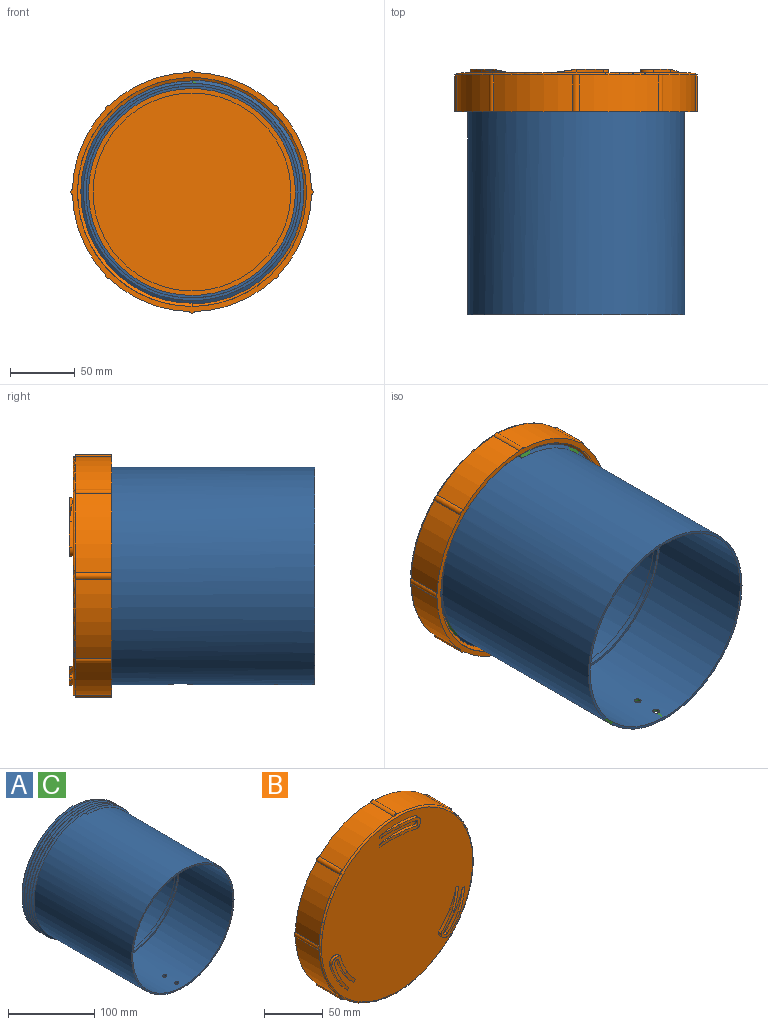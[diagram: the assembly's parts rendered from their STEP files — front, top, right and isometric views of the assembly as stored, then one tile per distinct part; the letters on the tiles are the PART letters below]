
ASSEMBLY  parts=3 mates=1
PART A: 20 faces, bbox 199.8x180x173 mm
  f0: cylinder r=84mm len=168mm, axis (0,1,0), area 83625.4mm2, adj f5,f8,f14,f15,f17,f18,f19
  f1: cylinder r=84mm len=168mm, axis (0,1,0), area 1055.6mm2, adj f2,f9,f13,f16
  f2: cylinder r=84mm len=168mm, axis (0,1,0), area 587.6mm2, adj f1,f3,f15,f16
  f3: cylinder r=84mm len=168mm, axis (0,1,0), area 587.6mm2, adj f2,f4,f15,f16
  f4: cylinder r=84mm len=168mm, axis (0,1,0), area 587.6mm2, adj f3,f5,f15,f16
  f5: cylinder r=84mm len=168mm, axis (0,1,0), area 587.6mm2, adj f0,f4,f15,f16
  f6: cylinder r=82mm len=164mm, axis (0,1,0), area 45300.5mm2, adj f8,f10,f18,f19
  f7: cylinder r=82mm len=164mm, axis (0,1,0), area 45025.2mm2, adj f9,f11,f17
  f8: plane 168x168mm, normal (0,-1,0), area 1043mm2, adj f0,f6
  f9: plane 168x168mm, normal (0,1,0), area 1043mm2, adj f1,f7
  f10: plane 164x164mm, normal (0,-1,0), area 1017.9mm2, adj f6,f12
  f11: plane 164x164mm, normal (0,1,0), area 1017.9mm2, adj f7,f12
  f12: cylinder r=80mm len=160mm, axis (0,1,0), area 2010.6mm2, adj f10,f11
  f13: plane 2.89x2.5mm, normal (1,0,0), area 3.6mm2, adj f1,f15,f16
  f14: plane 2.89x2.5mm, normal (-1,0,0), area 3.6mm2, adj f0,f15,f16
  f15: bspline ~199.76x173mm, area 7725.5mm2, adj f0,f2,f3,f4,f5,f13,f14,f16
  f16: bspline ~199.76x173mm, area 7731.3mm2, adj f1,f2,f3,f4,f5,f13,f14,f15
  f17: cylinder r=10mm len=20mm, axis (0,0,1), area 126.1mm2, adj f0,f7
  f18: cylinder r=2.5mm len=5mm, axis (0,0,1), area 31.4mm2, adj f0,f6
  f19: cylinder r=2.5mm len=5mm, axis (0,0,1), area 31.4mm2, adj f0,f6
PART B: 73 faces, bbox 207x35.6x202.9 mm
  f0: plane 182.02x182.02mm, normal (0,-1,0), area 25153.1mm2, adj f14,f35,f36,f37,f40,f41,f42,f43
  f1: cylinder r=92.5mm len=61.25mm, axis (0,1,0), area 1932.3mm2, adj f10,f14,f30,f32
  f2: cylinder r=92.5mm len=61.25mm, axis (0,1,0), area 1932.3mm2, adj f10,f14,f18,f32
  f3: cylinder r=92.5mm len=61.25mm, axis (0,1,0), area 1932.3mm2, adj f10,f14,f28,f30
  f4: cylinder r=92.5mm len=61.25mm, axis (0,1,0), area 1932.3mm2, adj f10,f14,f26,f28
  f5: cylinder r=92.5mm len=61.25mm, axis (0,1,0), area 1932.3mm2, adj f10,f14,f24,f26
  f6: cylinder r=92.5mm len=61.25mm, axis (0,1,0), area 1932.3mm2, adj f10,f14,f22,f24
  f7: cylinder r=92.5mm len=61.25mm, axis (0,1,0), area 1932.3mm2, adj f10,f14,f20,f22
  f8: cylinder r=92.5mm len=61.25mm, axis (0,1,0), area 1932.3mm2, adj f10,f14,f18,f20
  f9: cylinder r=88.5mm len=177mm, axis (0,1,0), area 5330.2mm2, adj f10,f11,f15,f16,f17
  f10: plane 187.4x187.4mm, normal (0,1,0), area 2307.2mm2, adj f1,f2,f3,f4,f5,f6,f7,f8
  f11: plane 178.62x177.65mm, normal (0,1,0), area 5788.2mm2, adj f9,f12,f16,f17
  f12: cylinder r=76.5mm len=153mm, axis (0,1,0), area 1442mm2, adj f11,f13
  f13: plane 153x153mm, normal (0,1,0), area 18385.4mm2, adj f12
  f14: torus R=91mm, axis (0,-1,0), area 1361.3mm2, adj f0,f1,f2,f3,f4,f5,f6,f7
  f15: plane 2.89x2.5mm, normal (1,0,0), area 3.6mm2, adj f9,f16,f17
  f16: bspline ~204.38x177mm, area 7672.4mm2, adj f9,f11,f15,f17
  f17: bspline ~204.38x177mm, area 7173.2mm2, adj f9,f11,f15,f16
  f18: cylinder r=3mm len=28.5mm, axis (0,1,0), area 161mm2, adj f2,f8,f10,f19
  f19: plane 4.85x1.23mm, normal (0,-1,0), area 4.1mm2, adj f14,f18
  f20: cylinder r=3mm len=28.5mm, axis (0,1,0), area 161mm2, adj f7,f8,f10,f21
  f21: plane 3.47x3.47mm, normal (0,-1,0), area 4.1mm2, adj f14,f20
  f22: cylinder r=3mm len=28.5mm, axis (0,1,0), area 161mm2, adj f6,f7,f10,f23
  f23: plane 4.85x1.23mm, normal (0,-1,0), area 4.1mm2, adj f14,f22
  f24: cylinder r=3mm len=28.5mm, axis (0,1,0), area 161mm2, adj f5,f6,f10,f25
  f25: plane 3.47x3.47mm, normal (0,-1,0), area 4.1mm2, adj f14,f24
  f26: cylinder r=3mm len=28.5mm, axis (0,1,0), area 161mm2, adj f4,f5,f10,f27
  f27: plane 4.85x1.23mm, normal (0,-1,0), area 4.1mm2, adj f14,f26
  f28: cylinder r=3mm len=28.5mm, axis (0,1,0), area 161mm2, adj f3,f4,f10,f29
  f29: plane 3.47x3.47mm, normal (0,-1,0), area 4.1mm2, adj f14,f28
  f30: cylinder r=3mm len=28.5mm, axis (0,1,0), area 161mm2, adj f1,f3,f10,f31
  f31: plane 4.85x1.23mm, normal (0,-1,0), area 4.1mm2, adj f14,f30
  f32: cylinder r=3mm len=28.5mm, axis (0,1,0), area 161mm2, adj f1,f2,f10,f33
  f33: plane 3.47x3.47mm, normal (0,-1,0), area 4.1mm2, adj f14,f32
  f34: plane 25.24x14.65mm, normal (0,-1,0), area 160mm2, adj f35,f36,f37,f38,f39,f40,f41,f42
  f35: cylinder r=84.5mm len=21.38mm, axis (0,-1,0), area 32.5mm2, adj f0,f34,f37,f44
  f36: cylinder r=81.5mm len=41.06mm, axis (0,-1,0), area 92.2mm2, adj f0,f34,f37,f38,f42
  f37: plane 21.4x5.68mm, normal (-0.13,-0.99,-0.04), area 64.3mm2, adj f0,f34,f35,f36,f38
  f38: plane 2.87x0.1mm, normal (-1,0,0), area 0.1mm2, adj f34,f36,f37
  f39: plane 2.73x0.11mm, normal (-1,0,0), area 0.1mm2, adj f34,f41,f46
  f40: cylinder r=76mm len=42.19mm, axis (0,-1,0), area 95.8mm2, adj f0,f34,f42,f46
  f41: bspline ~21.32x3.18mm, area 64.4mm2, adj f0,f34,f39,f43,f45
  f42: cylinder r=3.5mm len=5.79mm, axis (0,1,0), area 20.5mm2, adj f0,f34,f36,f40
  f43: bspline ~11.97x4.12mm, area 44.5mm2, adj f0,f34,f41,f44
  f44: bspline ~21.66x3mm, area 65.4mm2, adj f0,f34,f35,f43
  f45: cylinder r=73mm len=20.58mm, axis (0,-1,0), area 30.2mm2, adj f0,f41,f46
  f46: plane 21.45x5.99mm, normal (-0.13,-0.99,-0.04), area 64.5mm2, adj f0,f34,f39,f40,f45
  f47: plane 27.01x18.36mm, normal (0,-1,0), area 160mm2, adj f48,f49,f50,f51,f52,f53,f54,f55
  f48: cylinder r=84.5mm len=17.14mm, axis (0,-1,0), area 32.5mm2, adj f0,f47,f50,f57
  f49: cylinder r=81.5mm len=35.53mm, axis (0,-1,0), area 92.2mm2, adj f0,f47,f50,f51,f55
  f50: plane 18.67x15.21mm, normal (0.1,-0.99,-0.1), area 64.3mm2, adj f0,f47,f48,f49,f51
  f51: plane 2.48x1.43mm, normal (0.5,0,-0.87), area 0.1mm2, adj f47,f49,f50
  f52: plane 2.36x1.36mm, normal (0.5,0,-0.87), area 0.1mm2, adj f47,f54,f59
  f53: cylinder r=76mm len=36.44mm, axis (0,-1,0), area 95.8mm2, adj f0,f47,f55,f59
  f54: bspline ~20.05x7.91mm, area 64.4mm2, adj f0,f47,f52,f56,f58
  f55: cylinder r=3.5mm len=4.85mm, axis (0,1,0), area 20.5mm2, adj f0,f47,f49,f53
  f56: bspline ~10.59x7.03mm, area 44.5mm2, adj f0,f47,f54,f57
  f57: bspline ~20.17x8.39mm, area 65.4mm2, adj f0,f47,f48,f56
  f58: cylinder r=73mm len=16.34mm, axis (0,-1,0), area 30.2mm2, adj f0,f54,f59
  f59: plane 18.54x15.44mm, normal (0.1,-0.99,-0.1), area 64.5mm2, adj f0,f47,f52,f53,f58
  f60: plane 24.12x23.33mm, normal (0,-1,0), area 160mm2, adj f61,f62,f63,f64,f65,f66,f67,f68
  f61: cylinder r=84.5mm len=19.89mm, axis (0,-1,0), area 32.5mm2, adj f0,f60,f63,f70
  f62: cylinder r=81.5mm len=35.58mm, axis (0,-1,0), area 92.2mm2, adj f0,f60,f63,f64,f68
  f63: plane 20.68x10.93mm, normal (0.04,-0.99,0.13), area 64.3mm2, adj f0,f60,f61,f62,f64
  f64: plane 2.48x1.43mm, normal (0.5,0,0.87), area 0.1mm2, adj f60,f62,f63
  f65: plane 2.36x1.36mm, normal (0.5,0,0.87), area 0.1mm2, adj f60,f67,f72
  f66: cylinder r=76mm len=36.63mm, axis (0,-1,0), area 95.8mm2, adj f0,f60,f68,f72
  f67: bspline ~16.88x13.41mm, area 64.4mm2, adj f0,f60,f65,f69,f71
  f68: cylinder r=3.5mm len=5.18mm, axis (0,1,0), area 20.5mm2, adj f0,f60,f62,f66
  f69: bspline ~10.19x7.51mm, area 44.5mm2, adj f0,f60,f67,f70
  f70: bspline ~17.35x13.28mm, area 65.4mm2, adj f0,f60,f61,f69
  f71: cylinder r=73mm len=19.3mm, axis (0,-1,0), area 30.2mm2, adj f0,f67,f72
  f72: plane 20.76x10.67mm, normal (0.03,-0.99,0.14), area 64.5mm2, adj f0,f60,f65,f66,f71
PART C: same geometry as A
PLACE A t=(-0.25,79.68,-0.3)mm
PLACE B rot(axis=(1,0,0),180deg) t=(-0.25,56.68,-0.3)mm
PLACE C t=(-0.25,79.68,-0.3)mm
MATE fastened B.f1 <-> A.f0  axis (0,-1,0) through (-0.25,79.68,-0.3)mm
